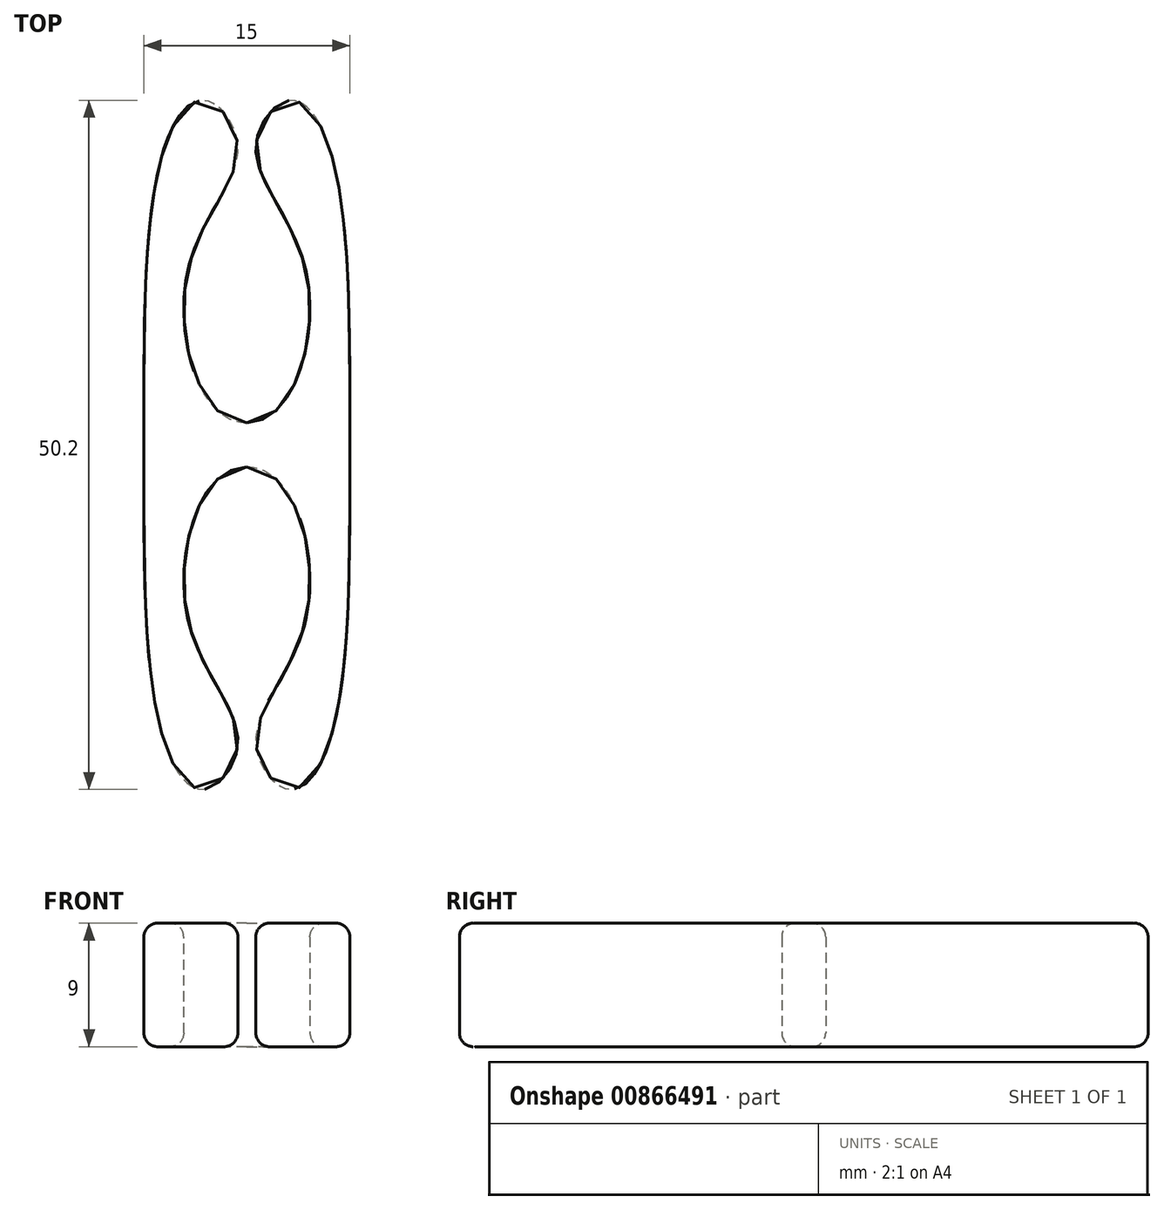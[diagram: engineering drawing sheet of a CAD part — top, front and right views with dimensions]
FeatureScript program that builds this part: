
annotation { "Feature Type Name" : "Feature", "Feature Type Description" : "" }
export const myFeature = defineFeature(function(context is Context, id is Id, definition is map)
    precondition{}
    {
        {
            var Q0;
            Q0=qCreatedBy(makeId("Top.planeOp"),FACE);
            var sketch = newSketch(context, id + "F0", { "sketchPlane" : qUnion([Q0])});
            skLineSegment(sketch, "E0", {"start": v(0, 25) * mm, "end": v(0, -25) * mm});
            skPoint(sketch, "E1", {"position": v(0, 0) * mm});
            skSolve(sketch);
        }
        {
            var Q0;
            Q0=qCreatedBy(makeId("Top.planeOp"),FACE);
            var sketch = newSketch(context, id + "F1", { "sketchPlane" : qUnion([Q0])});
            skFitSpline(sketch, "E2", {"points": [v(-7.5, 0) * mm, v(-6.13, 21.3) * mm, v(-3.08, 25.1) * mm, v(-0.65, 21.57) * mm, v(-4.4, 12.26) * mm, v(0, 1.6) * mm], "startDerivative": vector(0, 77.57) * mm, "endDerivative": vector(47.77, 0) * mm});
            skLineSegment(sketch, "E3", {"start": v(0, 1.6) * mm, "end": v(0, 0) * mm});
            skLineSegment(sketch, "E4", {"start": v(0, 0) * mm, "end": v(-7.5, 0) * mm});
            skSolve(sketch);
        }
        {
            var Q0;
            Q0 = qSketchRegion(id + "F1", true);
            extrude(context, id + "F2", {"entities" : qUnion([Q0]), "endBound" : BoundingType.SYMMETRIC, "depth" : 9 * mm, "offsetDistance" : 25 * mm});
        }
        {
            var Q0;
            Q0=makeQuery(id+"F2.opExtrude","SWEPT_BODY",BODY,{"disambiguationData":[OSD([sQuery(id+"F1.wireOp",EDGE,"E2"),sQuery(id+"F1.wireOp",EDGE,"E3"),sQuery(id+"F1.wireOp",EDGE,"E4")])]});
            var Q1;
            Q1=makeQuery(id+"F2.opExtrude","SWEPT_FACE",FACE,{"disambiguationData":[OSD([sQuery(id+"F1.wireOp",EDGE,"E3")])]});
            mirror(context, id + "F3", {"operationType" : NewBodyOperationType.ADD, "entities" : qUnion([Q0]), "mirrorPlane" : qUnion([Q1])});
        }
        {
            var Q0;
            Q0=makeQuery(id+"F2.opExtrude","SWEPT_BODY",BODY,{"disambiguationData":[OSD([sQuery(id+"F1.wireOp",EDGE,"E2"),sQuery(id+"F1.wireOp",EDGE,"E3"),sQuery(id+"F1.wireOp",EDGE,"E4")])]});
            var Q1;
            {var subQ0=makeQuery(id+"F2.opExtrude","SWEPT_FACE",FACE,{"disambiguationData":[OSD([sQuery(id+"F1.wireOp",EDGE,"E4")])]});Q1=makeQuery(id+"F3.boolean.opBoolean","MERGE",FACE,{"derivedFrom":[subQ0,makeQuery(id+"F3.opPattern","COPY",FACE,{"derivedFrom":subQ0,"instanceName":"1"})]});}
            mirror(context, id + "F4", {"operationType" : NewBodyOperationType.ADD, "entities" : qUnion([Q0]), "mirrorPlane" : qUnion([Q1])});
        }
        {
            var Q0;
            Q0=makeQuery(id+"F2.opExtrude","CAP_EDGE",EDGE,{"disambiguationData":[OSD([sQuery(id+"F1.wireOp",EDGE,"E2")])],"isStart":false});
            var Q1;
            Q1=makeQuery(id+"F4.opPattern","COPY",EDGE,{"derivedFrom":makeQuery(id+"F2.opExtrude","CAP_EDGE",EDGE,{"disambiguationData":[OSD([sQuery(id+"F1.wireOp",EDGE,"E2")])],"isStart":true}),"instanceName":"1"});
            fillet(context, id + "F5", {"entities" : qUnion([Q0, Q1]), "radius" : 1 * mm, "tangentPropagation" : true, "allowEdgeOverflow" : false});
        }
    });
